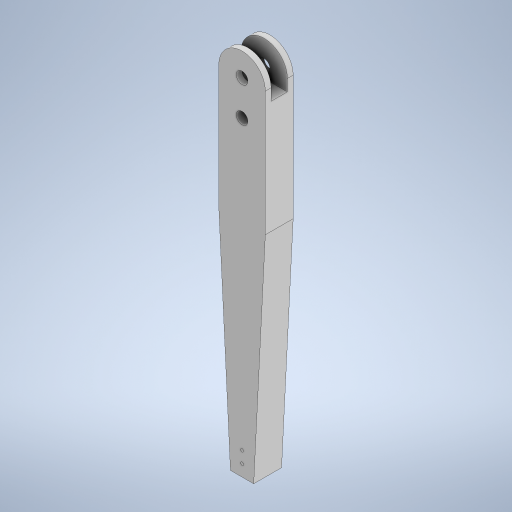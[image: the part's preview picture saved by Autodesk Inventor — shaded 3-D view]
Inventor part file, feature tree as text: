
AUTODESK INVENTOR PART (.ipt)
format: ipt  version: 2024.3 (Build 283343000, 343)  size: 291,328 bytes
history: native  units: mm
features: extrude x3, sketch x3, other x1, fillet x1
ambient origin geometry x8: Origin, YZ Plane, XZ Plane, XY Plane, X Axis, Y Axis, Z Axis, Center Point
bodies: Body1 (feature_tree)
feature tree (8):
  other  "ソリッド1"
  extrude  "押し出し1"  Depth=40.0mm
  extrude  "押し出し4"  Depth=318.0mm
  extrude  "押し出し5"  Depth=24.0mm TaperAngle=0.0deg
  fillet  "フィレット1"  Radius=10.0mm
  sketch  "スケッチ1"
  sketch  "スケッチ6"
  sketch  "スケッチ8"
